# Revit family: Kohler Loure 14675A-4-CP Family
name_source: partatom
category: Plumbing Fixtures
revit_build: Autodesk Revit 2018 (Build: 20170223_1515(x64)
units: mm (PartAtom-declared; Revit-internal decimal feet)

## family parameters
Cut with Voids When Loaded = No
Host = Face
Part Type = Normal
Room Calculation Point = No
Round Connector Dimension = Use Diameter
Shared = No

## types (1)
- Kohler Loure 14675A-4-CP Family
    Default Elevation = 1219 mm
    Description = LOURE DECK MOUNT BATH FAUCET
    Disclamer = Although care has been taken to ensure, to the best of our knowledge, that all data and information contained herein is accurate
to the extent that it relates to either matters of fact or accepted practice at the time of issue. MDFC (Pty) Ltd assumes no responsibility for
any errors in, or misinterpretation of, such data and/ or information or any loss or damage arising from, or related to its use.
    Faucet Height = 367 mm  [stored 1.20407 ft]
    Faucet Width = 165 mm
    Handle Height = 111 mm
    Handle Width = 108 mm  [stored 0.354331 ft]
    Manufacturer = Kohler CO
    Material = Faucets
    Model = 14675A-4-CP
    Telephone = 011 050 9000
    URL = http://www.africa.kohler.com

note: [stored X ft] marks values corroborated as IEEE doubles in the binary element streams (Revit-internal decimal feet)

## geometry (parser evidence)
native form markers: Sweep x2
no freeform markers — native parametric forms only
